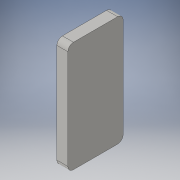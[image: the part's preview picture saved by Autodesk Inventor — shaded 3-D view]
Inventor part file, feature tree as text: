
AUTODESK INVENTOR PART (.ipt)
format: ipt  version: 2016 (Build 200138000, 138)  size: 99,840 bytes
history: native  units: in
note: dims shown in document units (in); Inventor stores cm internally (conversion verified against a paired STEP export)
features: fillet x4, extrude x1, sketch x1
ambient origin geometry x8: Origin, YZ Plane, XZ Plane, XY Plane, X Axis, Y Axis, Z Axis, Center Point
bodies: Solid1 (feature_tree)
feature tree (6):
  extrude  "Extrusion1"  Depth=2.5in
  fillet  "Fillet1"  Radius=0.5in
  fillet  "Fillet2"  Radius=0.25in
  fillet  "Fillet3"  Radius=0.25in
  fillet  "Fillet4"  Radius=0.25in
  sketch  "Sketch1"  dims[d0=5.0in d1=2.5in d2=0.5in d3=0.0in d4=0.25in d5=0.25in d6=0.25in d7=0.25in]
